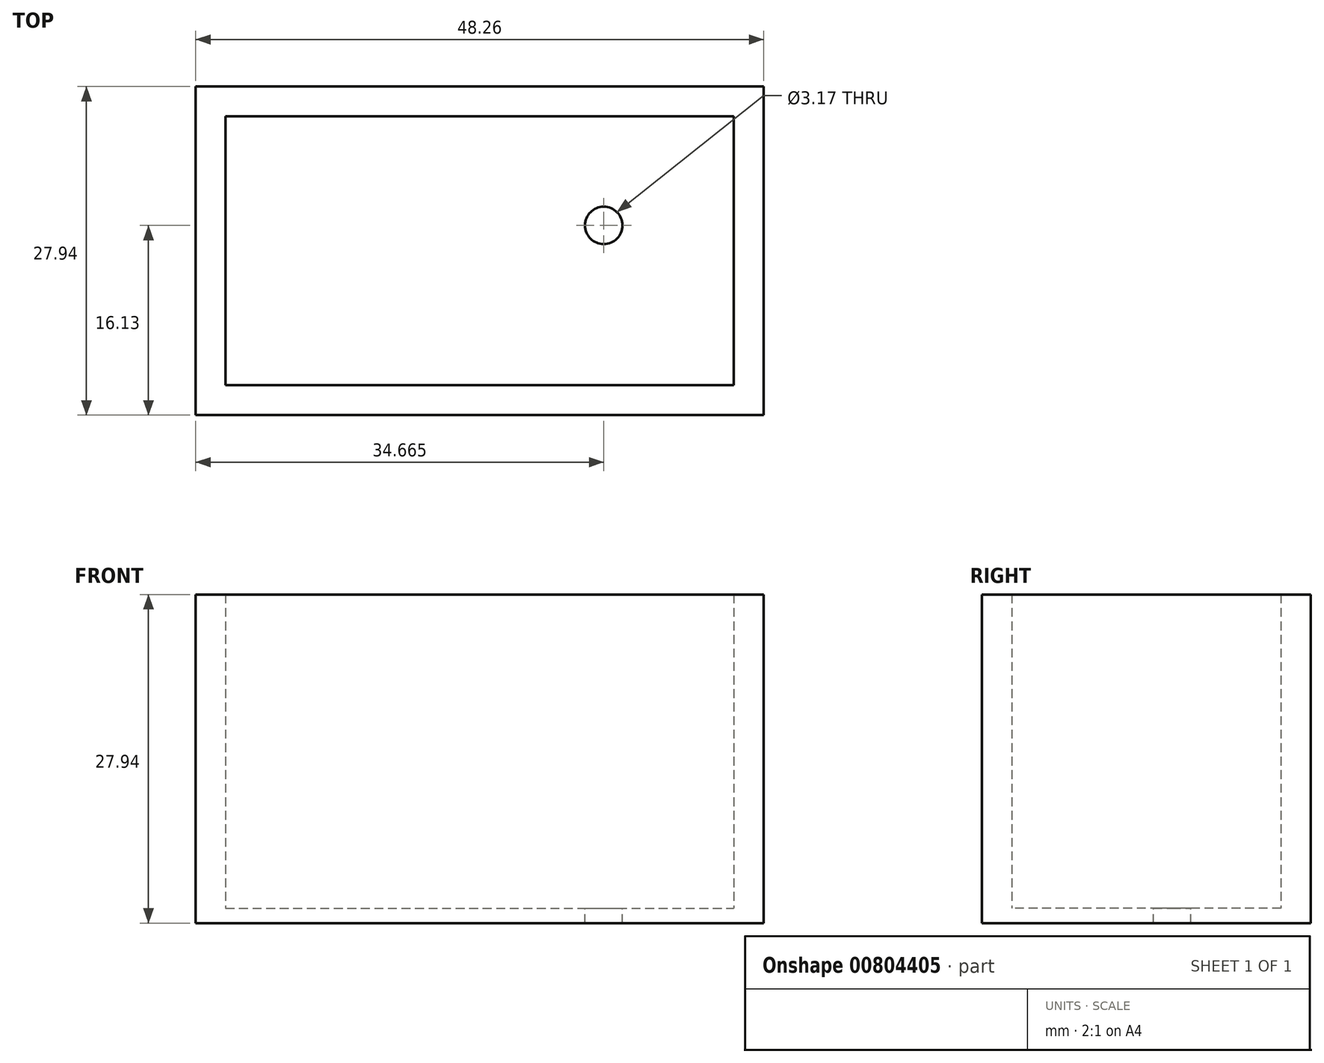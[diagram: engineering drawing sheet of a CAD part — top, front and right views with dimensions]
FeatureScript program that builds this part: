
annotation { "Feature Type Name" : "Feature", "Feature Type Description" : "" }
export const myFeature = defineFeature(function(context is Context, id is Id, definition is map)
    precondition{}
    {
        {
            var Q0;
            Q0=qCreatedBy(makeId("Top.planeOp"),FACE);
            var sketch = newSketch(context, id + "F0", { "sketchPlane" : qUnion([Q0])});
            skLineSegment(sketch, "E0.bottom", {"start": v(-43.18, 25.4) * mm, "end": v(0, 25.4) * mm});
            skLineSegment(sketch, "E0.top", {"start": v(-43.18, 2.54) * mm, "end": v(0, 2.54) * mm});
            skLineSegment(sketch, "E0.left", {"start": v(-43.18, 25.4) * mm, "end": v(-43.18, 2.54) * mm});
            skLineSegment(sketch, "E0.right", {"start": v(0, 25.4) * mm, "end": v(0, 2.54) * mm});
            skLineSegment(sketch, "E1", {"start": v(-43.18, 25.4) * mm, "end": v(-43.18, 27.94) * mm});
            skLineSegment(sketch, "E2", {"start": v(-43.18, 25.4) * mm, "end": v(-45.72, 25.4) * mm});
            skLineSegment(sketch, "E3", {"start": v(-43.18, 2.54) * mm, "end": v(-43.18, 0) * mm});
            skLineSegment(sketch, "E4", {"start": v(-43.18, 2.54) * mm, "end": v(-45.72, 2.54) * mm});
            skLineSegment(sketch, "E5", {"start": v(0, 25.4) * mm, "end": v(0, 27.94) * mm});
            skLineSegment(sketch, "E6", {"start": v(0, 25.4) * mm, "end": v(2.54, 25.4) * mm});
            skLineSegment(sketch, "E7", {"start": v(0, 2.54) * mm, "end": v(0, 0) * mm});
            skLineSegment(sketch, "E8", {"start": v(0, 2.54) * mm, "end": v(2.54, 2.54) * mm});
            skLineSegment(sketch, "E9", {"start": v(-45.72, 25.4) * mm, "end": v(-45.72, 0) * mm});
            skLineSegment(sketch, "E10", {"start": v(-45.72, 0) * mm, "end": v(0, 0) * mm});
            skLineSegment(sketch, "E11", {"start": v(0, 0) * mm, "end": v(2.54, 0) * mm});
            skLineSegment(sketch, "E12", {"start": v(2.54, 0) * mm, "end": v(2.54, 25.4) * mm});
            skLineSegment(sketch, "E13", {"start": v(2.54, 25.4) * mm, "end": v(2.54, 27.94) * mm});
            skLineSegment(sketch, "E14", {"start": v(2.54, 27.94) * mm, "end": v(-43.18, 27.94) * mm});
            skLineSegment(sketch, "E15", {"start": v(-43.18, 27.94) * mm, "end": v(-45.72, 27.94) * mm});
            skLineSegment(sketch, "E16", {"start": v(-45.72, 27.94) * mm, "end": v(-45.72, 25.4) * mm});
            skSolve(sketch);
        }
        {
            var Q0;
            Q0=makeQuery(id+"F0.imprint","IMPRINT",FACE,{"disambiguationData":[TD([[makeQuery(id+"F0.imprint","IMPRINT",EDGE,{"derivedFrom":sQuery(id+"F0.wireOp",EDGE,"E0.bottom")}),1.0]])]});
            var Q1;
            Q1=makeQuery(id+"F0.imprint","IMPRINT",FACE,{"disambiguationData":[TD([[makeQuery(id+"F0.imprint","IMPRINT",EDGE,{"derivedFrom":sQuery(id+"F0.wireOp",EDGE,"E1")}),1.0]])]});
            var Q2;
            Q2=makeQuery(id+"F0.imprint","IMPRINT",FACE,{"disambiguationData":[TD([[makeQuery(id+"F0.imprint","IMPRINT",EDGE,{"derivedFrom":sQuery(id+"F0.wireOp",EDGE,"E0.left")}),-1.0]])]});
            var Q3;
            {var subQ0=sQuery(id+"F0.wireOp",EDGE,"E3");Q3=makeQuery(id+"F0.imprint","IMPRINT",FACE,{"disambiguationData":[TD([[makeQuery(id+"F0.imprint","IMPRINT",EDGE,{"derivedFrom":subQ0}),-1.0]])]});}
            var Q4;
            Q4=makeQuery(id+"F0.imprint","IMPRINT",FACE,{"disambiguationData":[TD([[makeQuery(id+"F0.imprint","IMPRINT",EDGE,{"derivedFrom":sQuery(id+"F0.wireOp",EDGE,"E0.top")}),-1.0]])]});
            var Q5;
            Q5=makeQuery(id+"F0.imprint","IMPRINT",FACE,{"disambiguationData":[TD([[makeQuery(id+"F0.imprint","IMPRINT",EDGE,{"derivedFrom":sQuery(id+"F0.wireOp",EDGE,"E7")}),1.0]])]});
            var Q6;
            Q6=makeQuery(id+"F0.imprint","IMPRINT",FACE,{"disambiguationData":[TD([[makeQuery(id+"F0.imprint","IMPRINT",EDGE,{"derivedFrom":sQuery(id+"F0.wireOp",EDGE,"E0.right")}),1.0]])]});
            var Q7;
            {var subQ0=sQuery(id+"F0.wireOp",EDGE,"E5");Q7=makeQuery(id+"F0.imprint","IMPRINT",FACE,{"disambiguationData":[TD([[makeQuery(id+"F0.imprint","IMPRINT",EDGE,{"derivedFrom":subQ0}),-1.0]])]});}
            extrude(context, id + "F1", {"entities" : qUnion([Q0, Q1, Q2, Q3, Q4, Q5, Q6, Q7]), "depth" : 26.67 * mm, "offsetDistance" : 25.4 * mm});
        }
        {
            var Q0;
            Q0=makeQuery(id+"F1.opExtrude","CAP_FACE",FACE,{"disambiguationData":[OSD([sQuery(id+"F0.wireOp",EDGE,"E0.bottom"),sQuery(id+"F0.wireOp",EDGE,"E0.top"),sQuery(id+"F0.wireOp",EDGE,"E0.left"),sQuery(id+"F0.wireOp",EDGE,"E0.right"),sQuery(id+"F0.wireOp",EDGE,"E9"),sQuery(id+"F0.wireOp",EDGE,"E10"),sQuery(id+"F0.wireOp",EDGE,"E11"),sQuery(id+"F0.wireOp",EDGE,"E12"),sQuery(id+"F0.wireOp",EDGE,"E13"),sQuery(id+"F0.wireOp",EDGE,"E14"),sQuery(id+"F0.wireOp",EDGE,"E15"),sQuery(id+"F0.wireOp",EDGE,"E16")])],"isStart":true});
            var sketch = newSketch(context, id + "F2", { "sketchPlane" : qUnion([Q0])});
            skLineSegment(sketch, "E17.bottom", {"start": v(-45.72, 0) * mm, "end": v(2.54, 0) * mm});
            skLineSegment(sketch, "E17.top", {"start": v(-45.72, -27.94) * mm, "end": v(2.54, -27.94) * mm});
            skLineSegment(sketch, "E17.left", {"start": v(-45.72, 0) * mm, "end": v(-45.72, -27.94) * mm});
            skLineSegment(sketch, "E17.right", {"start": v(2.54, 0) * mm, "end": v(2.54, -27.94) * mm});
            skCircle(sketch, "E18", {"center": v(-11.05, -16.13) * mm, "radius": 1.59 * mm});
            skSolve(sketch);
        }
        {
            var Q0;
            Q0 = qSketchRegion(id + "F2", true);
            var Q1;
            Q1=makeQuery(id+"F2.imprint","IMPRINT",FACE,{"disambiguationData":[TD([[makeQuery(id+"F2.imprint","IMPRINT",EDGE,{"derivedFrom":makeQuery(id+"F1.opExtrude","CAP_EDGE",EDGE,{"disambiguationData":[OSD([sQuery(id+"F0.wireOp",EDGE,"E0.bottom")])],"isStart":true})}),1.0]])]});
            extrude(context, id + "F3", {"entities" : qUnion([Q0, Q1]), "operationType" : NewBodyOperationType.ADD, "depth" : 1.27 * mm, "offsetDistance" : 25.4 * mm});
        }
    });
